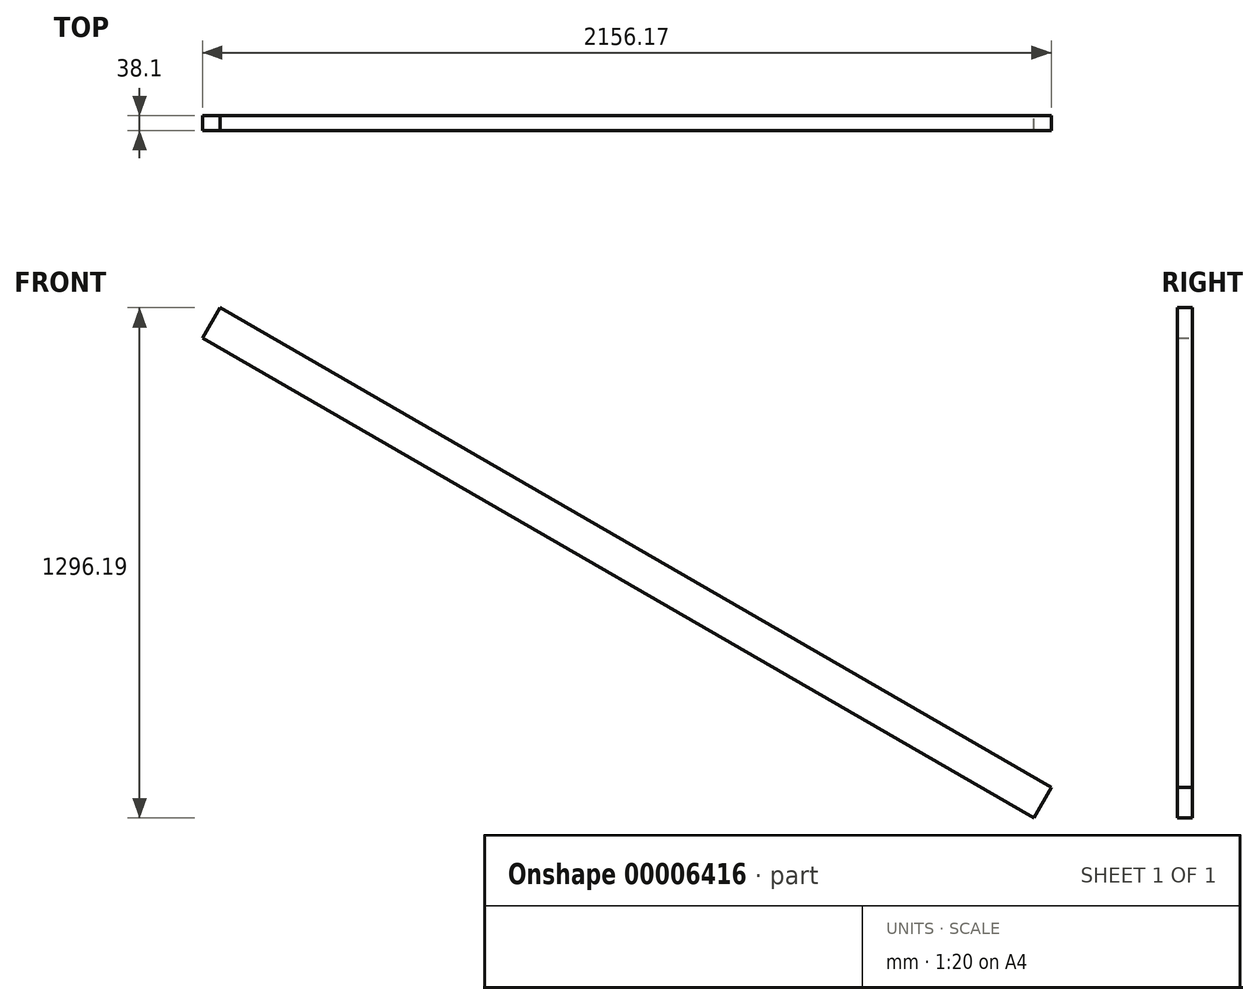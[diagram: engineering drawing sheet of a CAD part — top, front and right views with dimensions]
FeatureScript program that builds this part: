
annotation { "Feature Type Name" : "Feature", "Feature Type Description" : "" }
export const myFeature = defineFeature(function(context is Context, id is Id, definition is map)
    precondition{}
    {
        {
            var Q0;
            Q0=qCreatedBy(makeId("Front.planeOp"),FACE);
            var sketch = newSketch(context, id + "F0", { "sketchPlane" : qUnion([Q0])});
            skLineSegment(sketch, "E0", {"start": v(-1086.06, 660.23) * mm, "end": v(1025.66, -558.97) * mm});
            skLineSegment(sketch, "E1", {"start": v(1025.66, -558.97) * mm, "end": v(1070.1, -481.98) * mm});
            skLineSegment(sketch, "E2", {"start": v(1070.1, -481.98) * mm, "end": v(-1041.6, 737.22) * mm});
            skLineSegment(sketch, "E3", {"start": v(-1041.6, 737.22) * mm, "end": v(-1086.06, 660.23) * mm});
            skSolve(sketch);
        }
        {
            var Q0;
            Q0=makeQuery(id+"F0.imprint","IMPRINT",FACE,{"disambiguationData":[TD([[makeQuery(id+"F0.imprint","IMPRINT",EDGE,{"derivedFrom":sQuery(id+"F0.wireOp",EDGE,"E0")}),1.0]])]});
            extrude(context, id + "F1", {"entities" : qUnion([Q0]), "depth" : 38.1 * mm});
        }
    });
